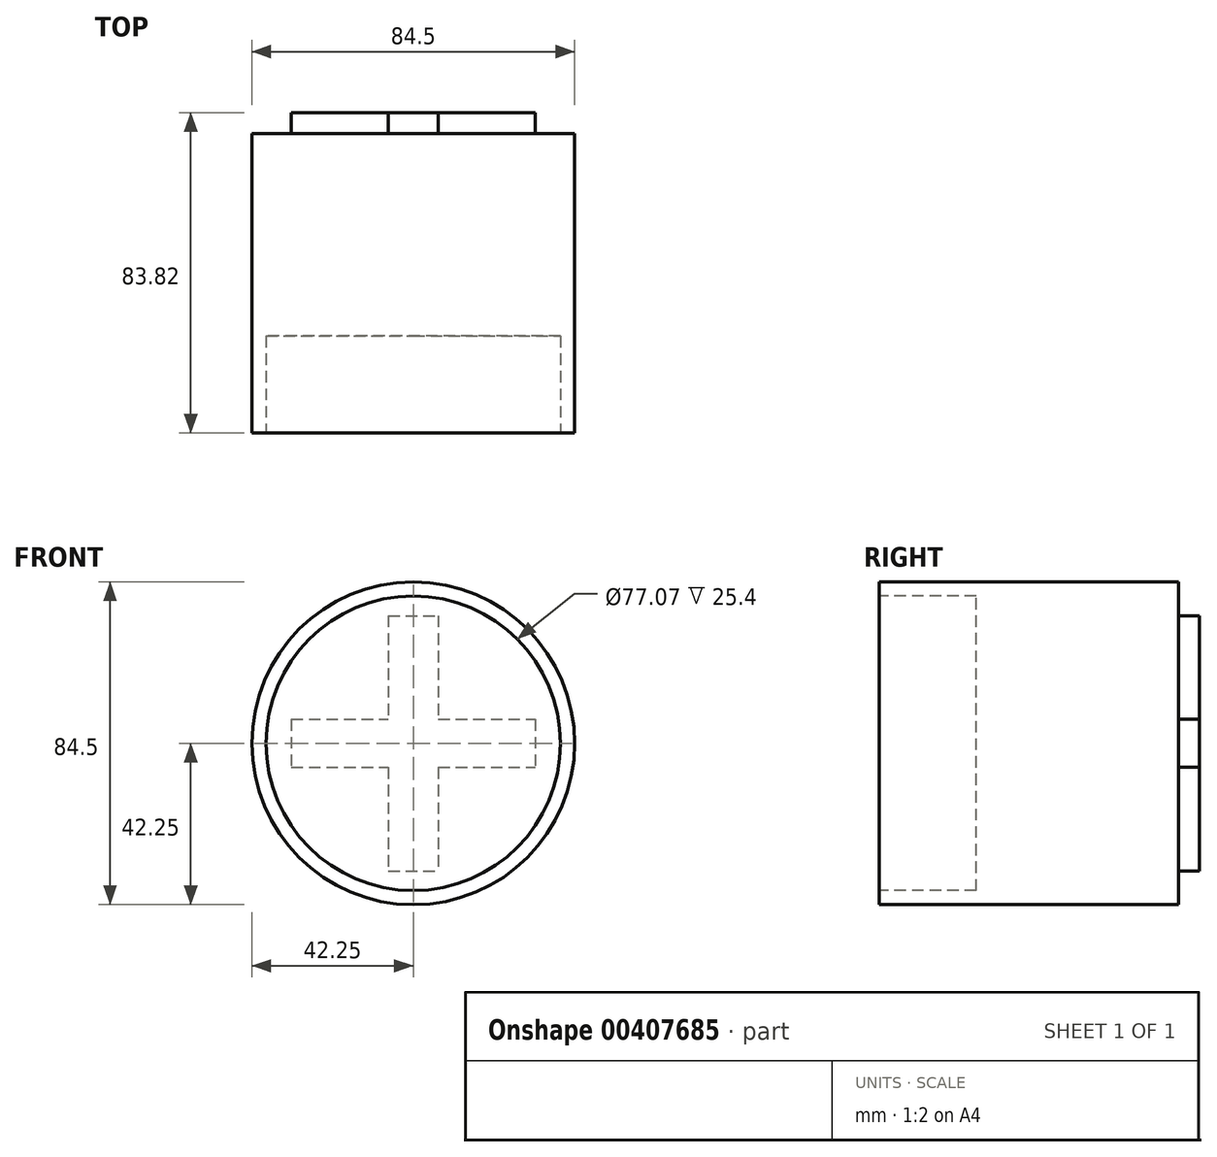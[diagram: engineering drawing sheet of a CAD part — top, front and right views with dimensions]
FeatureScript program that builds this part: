
annotation { "Feature Type Name" : "Feature", "Feature Type Description" : "" }
export const myFeature = defineFeature(function(context is Context, id is Id, definition is map)
    precondition{}
    {
        {
            var Q0;
            Q0=qCreatedBy(makeId("Front.planeOp"),FACE);
            var sketch = newSketch(context, id + "F0", { "sketchPlane" : qUnion([Q0])});
            skLineSegment(sketch, "E0", {"start": v(0, 0) * mm, "end": v(0, 42.25) * mm});
            skCircle(sketch, "E1", {"center": v(0, 0) * mm, "radius": 42.25 * mm});
            skSolve(sketch);
        }
        {
            var Q0;
            Q0=makeQuery(id+"F0.imprint","IMPRINT",FACE,{"disambiguationData":[TD([[makeQuery(id+"F0.imprint","IMPRINT",EDGE,{"derivedFrom":sQuery(id+"F0.wireOp",EDGE,"E1")}),1.0]])]});
            extrude(context, id + "F1", {"entities" : qUnion([Q0]), "depth" : 78.36 * mm});
        }
        {
            var Q0;
            Q0=makeQuery(id+"F1.opExtrude","CAP_FACE",FACE,{"disambiguationData":[OSD([sQuery(id+"F0.wireOp",EDGE,"E1")])],"isStart":false});
            var sketch = newSketch(context, id + "F2", { "sketchPlane" : qUnion([Q0])});
            skCircle(sketch, "E2", {"center": v(0, 0) * mm, "radius": 38.54 * mm});
            skSolve(sketch);
        }
        {
            var Q0;
            Q0=makeQuery(id+"F2.imprint","IMPRINT",FACE,{"disambiguationData":[TD([[makeQuery(id+"F2.imprint","IMPRINT",EDGE,{"derivedFrom":sQuery(id+"F2.wireOp",EDGE,"E2")}),1.0]])]});
            extrude(context, id + "F3", {"entities" : qUnion([Q0]), "operationType" : NewBodyOperationType.REMOVE, "oppositeDirection" : true, "depth" : 25.4 * mm});
        }
        {
            var Q0;
            Q0=makeQuery(id+"F1.opExtrude","CAP_FACE",FACE,{"disambiguationData":[OSD([sQuery(id+"F0.wireOp",EDGE,"E1")])],"isStart":true});
            var sketch = newSketch(context, id + "F4", { "sketchPlane" : qUnion([Q0])});
            skSolve(sketch);
        }
        {
            var Q0;
            Q0=makeQuery(id+"F4.imprint","IMPRINT",FACE,{"disambiguationData":[TD([[makeQuery(id+"F4.imprint","IMPRINT",EDGE,{"derivedFrom":makeQuery(id+"F1.opExtrude","CAP_EDGE",EDGE,{"disambiguationData":[OSD([sQuery(id+"F0.wireOp",EDGE,"E1")])],"isStart":true})}),-1.0]])]});
            var sketch = newSketch(context, id + "F5", { "sketchPlane" : qUnion([Q0])});
            skLineSegment(sketch, "E3.bottom", {"start": v(6.53, 33.39) * mm, "end": v(-6.53, 33.39) * mm});
            skLineSegment(sketch, "E3.top", {"start": v(6.53, -33.39) * mm, "end": v(-6.53, -33.39) * mm});
            skLineSegment(sketch, "E3.left", {"start": v(6.53, 33.39) * mm, "end": v(6.53, -33.39) * mm});
            skLineSegment(sketch, "E3.right", {"start": v(-6.53, 33.39) * mm, "end": v(-6.53, -33.39) * mm});
            skPoint(sketch, "E3.middle", {"position": v(0, 0) * mm});
            skLineSegment(sketch, "E4.bottom", {"start": v(31.9, 6.28) * mm, "end": v(-31.9, 6.28) * mm});
            skLineSegment(sketch, "E4.top", {"start": v(31.9, -6.28) * mm, "end": v(-31.9, -6.28) * mm});
            skLineSegment(sketch, "E4.left", {"start": v(31.9, 6.28) * mm, "end": v(31.9, -6.28) * mm});
            skLineSegment(sketch, "E4.right", {"start": v(-31.9, 6.28) * mm, "end": v(-31.9, -6.28) * mm});
            skSolve(sketch);
        }
        {
            var Q0;
            {var subQ0=sQuery(id+"F5.wireOp",EDGE,"E3.bottom");Q0=makeQuery(id+"F5.imprint","IMPRINT",FACE,{"disambiguationData":[TD([[makeQuery(id+"F5.imprint","IMPRINT",EDGE,{"derivedFrom":subQ0}),1.0]])]});}
            var Q1;
            {var subQ5=sQuery(id+"F5.wireOp",EDGE,"E4.left");Q1=makeQuery(id+"F5.imprint","IMPRINT",FACE,{"disambiguationData":[TD([[makeQuery(id+"F5.imprint","IMPRINT",EDGE,{"derivedFrom":subQ5}),-1.0]])]});}
            var Q2;
            {var subQ0=sQuery(id+"F5.wireOp",EDGE,"E3.top");Q2=makeQuery(id+"F5.imprint","IMPRINT",FACE,{"disambiguationData":[TD([[makeQuery(id+"F5.imprint","IMPRINT",EDGE,{"derivedFrom":subQ0}),-1.0]])]});}
            var Q3;
            {var subQ5=sQuery(id+"F5.wireOp",EDGE,"E4.right");Q3=makeQuery(id+"F5.imprint","IMPRINT",FACE,{"disambiguationData":[TD([[makeQuery(id+"F5.imprint","IMPRINT",EDGE,{"derivedFrom":subQ5}),1.0]])]});}
            var Q4;
            {var subQ0=sQuery(id+"F5.wireOp",EDGE,"E4.bottom");var subQ1=sQuery(id+"F5.wireOp",EDGE,"E3.left");var subQ2=makeQuery(id+"F5.imprint","INTERSECT",VERTEX,{"derivedFrom":[subQ1,subQ0]});Q4=makeQuery(id+"F5.imprint","IMPRINT",FACE,{"disambiguationData":[TD([[makeQuery(id+"F5.imprint","IMPRINT",EDGE,{"disambiguationData":[TD([[subQ2,-1.0]])],"derivedFrom":subQ1}),-1.0]])]});}
            extrude(context, id + "F6", {"entities" : qUnion([Q0, Q1, Q2, Q3, Q4]), "operationType" : NewBodyOperationType.ADD, "depth" : 5.46 * mm});
        }
    });
